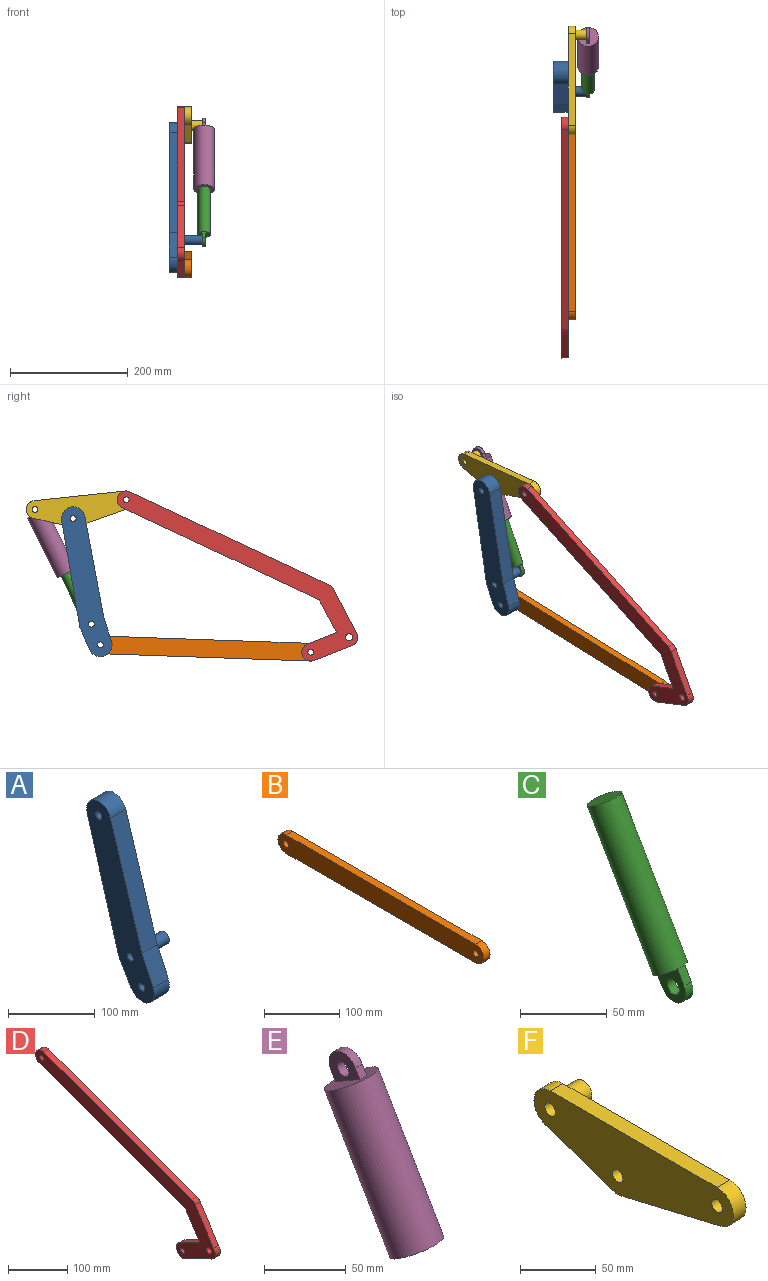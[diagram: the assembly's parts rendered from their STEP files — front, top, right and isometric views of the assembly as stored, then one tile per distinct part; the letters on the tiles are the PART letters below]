
ASSEMBLY  parts=6 mates=7
PART A: 14 faces, bbox 56x110.4x247.8 mm
  f0: cylinder r=20mm len=39.11mm, axis (1,0,0), area 1563.2mm2, adj f1,f6,f10,f11
  f1: plane 165.63x51.29mm, normal (0,-0.96,0.3), area 4334.9mm2, adj f0,f2,f10,f11
  f2: plane 39.71x25mm, normal (0,-0.91,0.42), area 1091.9mm2, adj f1,f3,f10,f11
  f3: cylinder r=20mm len=37.3mm, axis (1,0,0), area 1522.5mm2, adj f2,f4,f10,f11
  f4: plane 33.04x25mm, normal (0,0.86,-0.5), area 955.1mm2, adj f3,f5,f10,f11
  f5: cylinder r=20mm len=25mm, axis (1,0,0), area 120.4mm2, adj f4,f6,f10,f11
  f6: plane 174.72x51.22mm, normal (0,0.96,-0.28), area 4551.7mm2, adj f0,f5,f10,f11
  f7: cylinder r=5mm len=25mm, axis (1,0,0), area 785.4mm2, adj f10,f11
  f8: cylinder r=5mm len=25mm, axis (1,0,0), area 785.4mm2, adj f10,f11
  f9: cylinder r=5mm len=56mm, axis (1,0,0), area 1759.3mm2, adj f10,f12
  f10: plane 247.76x110.4mm, normal (-1,0,0), area 10143.6mm2, adj f0,f1,f2,f3,f4,f5,f6,f7
  f11: plane 247.76x110.4mm, normal (1,0,0), area 10021.1mm2, adj f0,f1,f2,f3,f4,f5,f6,f7
  f12: plane 16x16mm, normal (1,0,0), area 122.5mm2, adj f9,f13
  f13: cylinder r=8mm len=31mm, axis (-1,0,0), area 1558.2mm2, adj f11,f12
PART B: 8 faces, bbox 12x387.4x30 mm
  f0: plane 357.42x12mm, normal (0,0,1), area 4289.1mm2, adj f1,f4,f6,f7
  f1: cylinder r=15mm len=30mm, axis (-1,0,0), area 565.5mm2, adj f0,f2,f6,f7
  f2: plane 357.42x12mm, normal (0,0,-1), area 4289.1mm2, adj f1,f4,f6,f7
  f3: cylinder r=5mm len=12mm, axis (-1,0,0), area 377mm2, adj f6,f7
  f4: cylinder r=15mm len=30mm, axis (-1,0,0), area 565.5mm2, adj f0,f2,f6,f7
  f5: cylinder r=5mm len=12mm, axis (-1,0,0), area 377mm2, adj f6,f7
  f6: plane 387.42x30mm, normal (1,0,0), area 11272.5mm2, adj f0,f1,f2,f3,f4,f5
  f7: plane 387.42x30mm, normal (-1,0,0), area 11272.5mm2, adj f0,f1,f2,f3,f4,f5
PART C: 9 faces, bbox 21.3x78.5x117.3 mm
  f0: cylinder r=10.65mm len=103.23mm, axis (0,0.5,0.86), area 7159.3mm2, adj f1,f2
  f1: plane 21.3x18.42mm, normal (0,-0.5,-0.86), area 234.9mm2, adj f0,f3,f6,f7,f8
  f2: plane 21.3x18.42mm, normal (0,0.5,0.86), area 356.3mm2, adj f0
  f3: plane 9.3x6mm, normal (0,-0.86,0.5), area 64.5mm2, adj f1,f4,f7,f8
  f4: cylinder r=10.11mm len=18.86mm, axis (-1,0,0), area 190.7mm2, adj f3,f6,f7,f8
  f5: cylinder r=5mm len=10mm, axis (-1,0,0), area 188.5mm2, adj f7,f8
  f6: plane 9.3x6mm, normal (0,0.86,-0.5), area 64.5mm2, adj f1,f4,f7,f8
  f7: plane 24.5x24.26mm, normal (1,0,0), area 299.8mm2, adj f1,f3,f4,f5,f6
  f8: plane 24.5x24.26mm, normal (-1,0,0), area 299.8mm2, adj f1,f3,f4,f5,f6
PART D: 15 faces, bbox 12x427.7x259.8 mm
  f0: plane 68.21x43.84mm, normal (0,-0.84,0.54), area 973mm2, adj f1,f11,f13,f14
  f1: cylinder r=15mm len=24.13mm, axis (1,0,0), area 342.6mm2, adj f0,f2,f13,f14
  f2: plane 62.49x31.21mm, normal (0,-0.45,-0.89), area 838.2mm2, adj f1,f3,f13,f14
  f3: cylinder r=15mm len=28.42mm, axis (1,0,0), area 565.5mm2, adj f2,f4,f13,f14
  f4: plane 47.47x23.71mm, normal (0,0.45,0.89), area 636.7mm2, adj f3,f5,f13,f14
  f5: plane 52.52x34.09mm, normal (0,0.84,-0.54), area 751.3mm2, adj f4,f6,f13,f14
  f6: plane 348.54x126.77mm, normal (0,0.34,-0.94), area 4450.6mm2, adj f5,f7,f13,f14
  f7: cylinder r=15mm len=28.42mm, axis (1,0,0), area 538.4mm2, adj f6,f8,f13,f14
  f8: plane 352.2x127.99mm, normal (0,-0.34,0.94), area 4496.8mm2, adj f7,f11,f13,f14
  f9: cylinder r=5mm len=12mm, axis (1,0,0), area 377mm2, adj f13,f14
  f10: cylinder r=6mm len=12mm, axis (1,0,0), area 452.4mm2, adj f13,f14
  f11: cylinder r=15mm len=12mm, axis (1,0,0), area 117.2mm2, adj f0,f8,f13,f14
  f12: cylinder r=5mm len=12mm, axis (1,0,0), area 377mm2, adj f13,f14
  f13: plane 427.65x259.84mm, normal (-1,0,0), area 16190.3mm2, adj f0,f1,f2,f3,f4,f5,f6,f7
  f14: plane 427.65x259.84mm, normal (1,0,0), area 16190.3mm2, adj f0,f1,f2,f3,f4,f5,f6,f7
PART E: 15 faces, bbox 35.3x88.1x125.5 mm
  f0: plane 17.67x10.26mm, normal (0,-0.5,-0.86), area 115.1mm2, adj f1,f6
  f1: cylinder r=10.65mm len=104.18mm, axis (0,-0.5,-0.86), area 7031.4mm2, adj f0,f4,f5,f6,f7,f8
  f2: cylinder r=17.66mm len=115.46mm, axis (0,-0.5,-0.86), area 12539.8mm2, adj f3,f4
  f3: plane 35.32x30.55mm, normal (0,0.5,0.86), area 833.8mm2, adj f2,f9,f10,f11,f12
  f4: plane 35.32x30.55mm, normal (0,-0.5,-0.86), area 623.7mm2, adj f1,f2
  f5: plane 17.67x10.26mm, normal (0,-0.5,-0.86), area 115.1mm2, adj f1,f7
  f6: plane 26.03x24.52mm, normal (-1,0,0), area 338.5mm2, adj f0,f1,f8
  f7: plane 26.03x24.52mm, normal (1,0,0), area 338.5mm2, adj f1,f5,f8
  f8: plane 18.5x10.56mm, normal (0,-0.5,-0.87), area 126.1mm2, adj f1,f6,f7
  f9: plane 6.75x6mm, normal (0,0.86,-0.5), area 46.9mm2, adj f3,f11,f12,f13
  f10: plane 6.75x6mm, normal (0,-0.86,0.5), area 46.9mm2, adj f3,f11,f12,f13
  f11: plane 26.63x25.05mm, normal (1,0,0), area 344.6mm2, adj f3,f9,f10,f13,f14
  f12: plane 26.63x25.05mm, normal (-1,0,0), area 344.6mm2, adj f3,f9,f10,f13,f14
  f13: cylinder r=12.18mm len=22.71mm, axis (-1,0,0), area 229.6mm2, adj f9,f10,f11,f12
  f14: cylinder r=5mm len=10mm, axis (-1,0,0), area 188.5mm2, adj f11,f12
PART F: 15 faces, bbox 31x185.7x52.1 mm
  f0: plane 185.7x52.08mm, normal (1,0,0), area 6830.3mm2, adj f1,f2,f3,f4,f5,f6,f7,f8
  f1: plane 63.05x22.08mm, normal (0,0.33,-0.94), area 801.6mm2, adj f0,f2,f6,f10
  f2: cylinder r=15mm len=29.16mm, axis (-1,0,0), area 504.8mm2, adj f0,f1,f3,f10
  f3: plane 155.7x12mm, normal (0,0,1), area 1868.4mm2, adj f0,f2,f4,f10
  f4: cylinder r=15mm len=29.59mm, axis (-1,0,0), area 523.5mm2, adj f0,f3,f5,f10
  f5: plane 91.16x21.64mm, normal (0,-0.23,-0.97), area 1124.4mm2, adj f0,f4,f6,f10
  f6: cylinder r=15mm len=12mm, axis (-1,0,0), area 121.3mm2, adj f0,f1,f5,f10
  f7: cylinder r=5mm len=12mm, axis (-1,0,0), area 377mm2, adj f0,f10
  f8: cylinder r=5mm len=12mm, axis (-1,0,0), area 377mm2, adj f0,f10
  f9: cylinder r=5mm len=31mm, axis (-1,0,0), area 973.9mm2, adj f10,f11
  f10: plane 185.7x52.08mm, normal (-1,0,0), area 6952.9mm2, adj f1,f2,f3,f4,f5,f6,f7,f8
  f11: plane 16x16mm, normal (1,0,0), area 122.1mm2, adj f9,f12,f14
  f12: plane 14.66x3.01mm, normal (0,-0.5,-0.86), area 50.9mm2, adj f11,f13,f14
  f13: cylinder r=17.66mm len=3.11mm, axis (0,-0.5,-0.86), area 0.4mm2, adj f12,f14
  f14: cylinder r=8mm len=19mm, axis (-1,0,0), area 903.7mm2, adj f0,f11,f12,f13
PLACE A rot(axis=(1,0,0),6.6deg) t=(-49.99,277.08,-191.15)mm fixed
PLACE B rot(axis=(1,0,0),2deg) t=(-49.99,277.08,-191.15)mm
PLACE C rot(axis=(1,0,0),4deg) t=(-49.99,275.47,-190.4)mm
PLACE D rot(axis=(1,0,0),5.1deg) t=(-49.99,275.88,-171.87)mm
PLACE E rot(axis=(1,0,0),4deg) t=(-49.99,270.82,-199.85)mm
PLACE F rot(axis=(-1,0,0),6.1deg) t=(-49.99,231.14,-175.83)mm
MATE revolute A.f5 <-> C.f4  axis (1,0,0) through (-18.99,292.33,-156.12)mm
MATE revolute D.f7 <-> F.f4  axis (1,0,0) through (-49.99,233.25,55.07)mm
MATE revolute A.f8 <-> B.f3  axis (1,0,0) through (-49.99,277.08,-191.15)mm
MATE slider E.f1 <-> C.f0  axis (0,-0.44,-0.9) through (-15.99,334.78,-69.77)mm
MATE revolute D.f3 <-> B.f1  axis (1,0,0) through (-49.99,-80.12,-203.69)mm
MATE revolute F.f2 <-> E.f13  axis (1,0,0) through (-18.99,388.08,38.65)mm
MATE revolute F.f6 <-> A.f0  axis (-1,0,0) through (-49.99,323.06,23.34)mm
